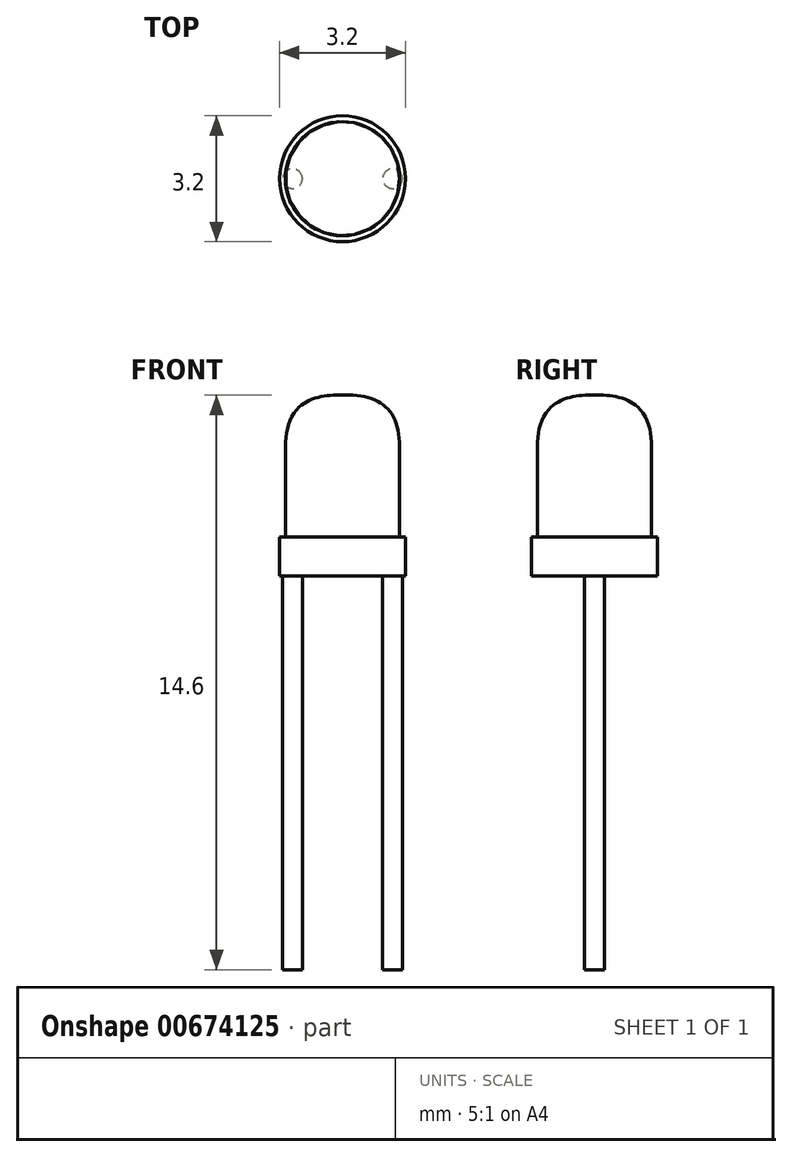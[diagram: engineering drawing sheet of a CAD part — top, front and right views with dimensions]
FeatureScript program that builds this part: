
annotation { "Feature Type Name" : "Feature", "Feature Type Description" : "" }
export const myFeature = defineFeature(function(context is Context, id is Id, definition is map)
    precondition{}
    {
        {
            var Q0;
            Q0=qCreatedBy(makeId("Top.planeOp"),FACE);
            var sketch = newSketch(context, id + "F0", { "sketchPlane" : qUnion([Q0])});
            skCircle(sketch, "E0", {"center": v(0, 0) * mm, "radius": 1.6 * mm});
            skCircle(sketch, "E1", {"center": v(0, 0) * mm, "radius": 1.45 * mm});
            skCircle(sketch, "E2", {"center": v(-1.27, 0) * mm, "radius": 0.25 * mm});
            skCircle(sketch, "E3", {"center": v(1.27, 0) * mm, "radius": 0.25 * mm});
            skSolve(sketch);
        }
        {
            var Q0;
            Q0=makeQuery(id+"F0.imprint","IMPRINT",FACE,{"disambiguationData":[TD([[makeQuery(id+"F0.imprint","IMPRINT",EDGE,{"derivedFrom":sQuery(id+"F0.wireOp",EDGE,"E0")}),1.0]])]});
            var Q1;
            {var subQ0=sQuery(id+"F0.wireOp",EDGE,"E2");var subQ1=sQuery(id+"F0.wireOp",EDGE,"E1");var subQ2=makeQuery(id+"F0.imprint","INTERSECT",VERTEX,{"disambiguationData":[OD(0.0)],"derivedFrom":[subQ1,subQ0]});Q1=makeQuery(id+"F0.imprint","IMPRINT",FACE,{"disambiguationData":[TD([[makeQuery(id+"F0.imprint","IMPRINT",EDGE,{"disambiguationData":[TD([[subQ2,1.0]])],"derivedFrom":subQ1}),1.0]])]});}
            var Q2;
            {var subQ0=sQuery(id+"F0.wireOp",EDGE,"E2");var subQ1=sQuery(id+"F0.wireOp",EDGE,"E1");var subQ2=makeQuery(id+"F0.imprint","INTERSECT",VERTEX,{"disambiguationData":[OD(0.0)],"derivedFrom":[subQ1,subQ0]});Q2=makeQuery(id+"F0.imprint","IMPRINT",FACE,{"disambiguationData":[TD([[makeQuery(id+"F0.imprint","IMPRINT",EDGE,{"disambiguationData":[TD([[subQ2,-1.0]])],"derivedFrom":subQ1}),1.0]])]});}
            var Q3;
            {var subQ0=sQuery(id+"F0.wireOp",EDGE,"E3");var subQ1=sQuery(id+"F0.wireOp",EDGE,"E1");var subQ2=makeQuery(id+"F0.imprint","INTERSECT",VERTEX,{"disambiguationData":[OD(0.0)],"derivedFrom":[subQ1,subQ0]});Q3=makeQuery(id+"F0.imprint","IMPRINT",FACE,{"disambiguationData":[TD([[makeQuery(id+"F0.imprint","IMPRINT",EDGE,{"disambiguationData":[TD([[subQ2,1.0]])],"derivedFrom":subQ1}),1.0]])]});}
            var Q4;
            {var subQ0=sQuery(id+"F0.wireOp",EDGE,"E3");var subQ1=sQuery(id+"F0.wireOp",EDGE,"E1");var subQ2=makeQuery(id+"F0.imprint","INTERSECT",VERTEX,{"disambiguationData":[OD(0.0)],"derivedFrom":[subQ1,subQ0]});Q4=makeQuery(id+"F0.imprint","IMPRINT",FACE,{"disambiguationData":[TD([[makeQuery(id+"F0.imprint","IMPRINT",EDGE,{"disambiguationData":[TD([[subQ2,1.0]])],"derivedFrom":subQ1}),-1.0]])]});}
            var Q5;
            {var subQ0=sQuery(id+"F0.wireOp",EDGE,"E2");var subQ1=sQuery(id+"F0.wireOp",EDGE,"E1");var subQ2=makeQuery(id+"F0.imprint","INTERSECT",VERTEX,{"disambiguationData":[OD(0.0)],"derivedFrom":[subQ1,subQ0]});Q5=makeQuery(id+"F0.imprint","IMPRINT",FACE,{"disambiguationData":[TD([[makeQuery(id+"F0.imprint","IMPRINT",EDGE,{"disambiguationData":[TD([[subQ2,-1.0]])],"derivedFrom":subQ1}),-1.0]])]});}
            extrude(context, id + "F1", {"entities" : qUnion([Q0, Q1, Q2, Q3, Q4, Q5]), "depth" : 1 * mm, "offsetDistance" : 25 * mm});
        }
        {
            var Q0;
            {var subQ0=sQuery(id+"F0.wireOp",EDGE,"E2");var subQ1=sQuery(id+"F0.wireOp",EDGE,"E1");var subQ2=makeQuery(id+"F0.imprint","INTERSECT",VERTEX,{"disambiguationData":[OD(0.0)],"derivedFrom":[subQ1,subQ0]});Q0=makeQuery(id+"F0.imprint","IMPRINT",FACE,{"disambiguationData":[TD([[makeQuery(id+"F0.imprint","IMPRINT",EDGE,{"disambiguationData":[TD([[subQ2,-1.0]])],"derivedFrom":subQ1}),-1.0]])]});}
            var Q1;
            {var subQ0=sQuery(id+"F0.wireOp",EDGE,"E2");var subQ1=sQuery(id+"F0.wireOp",EDGE,"E1");var subQ2=makeQuery(id+"F0.imprint","INTERSECT",VERTEX,{"disambiguationData":[OD(0.0)],"derivedFrom":[subQ1,subQ0]});Q1=makeQuery(id+"F0.imprint","IMPRINT",FACE,{"disambiguationData":[TD([[makeQuery(id+"F0.imprint","IMPRINT",EDGE,{"disambiguationData":[TD([[subQ2,-1.0]])],"derivedFrom":subQ1}),1.0]])]});}
            var Q2;
            {var subQ0=sQuery(id+"F0.wireOp",EDGE,"E3");var subQ1=sQuery(id+"F0.wireOp",EDGE,"E1");var subQ2=makeQuery(id+"F0.imprint","INTERSECT",VERTEX,{"disambiguationData":[OD(0.0)],"derivedFrom":[subQ1,subQ0]});Q2=makeQuery(id+"F0.imprint","IMPRINT",FACE,{"disambiguationData":[TD([[makeQuery(id+"F0.imprint","IMPRINT",EDGE,{"disambiguationData":[TD([[subQ2,1.0]])],"derivedFrom":subQ1}),1.0]])]});}
            var Q3;
            {var subQ0=sQuery(id+"F0.wireOp",EDGE,"E3");var subQ1=sQuery(id+"F0.wireOp",EDGE,"E1");var subQ2=makeQuery(id+"F0.imprint","INTERSECT",VERTEX,{"disambiguationData":[OD(0.0)],"derivedFrom":[subQ1,subQ0]});Q3=makeQuery(id+"F0.imprint","IMPRINT",FACE,{"disambiguationData":[TD([[makeQuery(id+"F0.imprint","IMPRINT",EDGE,{"disambiguationData":[TD([[subQ2,1.0]])],"derivedFrom":subQ1}),-1.0]])]});}
            extrude(context, id + "F2", {"entities" : qUnion([Q0, Q1, Q2, Q3]), "operationType" : NewBodyOperationType.ADD, "depth" : -10 * mm, "offsetDistance" : 25 * mm});
        }
        {
            var Q0;
            {var subQ0=sQuery(id+"F0.wireOp",EDGE,"E2");var subQ1=sQuery(id+"F0.wireOp",EDGE,"E1");var subQ2=makeQuery(id+"F0.imprint","INTERSECT",VERTEX,{"disambiguationData":[OD(0.0)],"derivedFrom":[subQ1,subQ0]});Q0=makeQuery(id+"F0.imprint","IMPRINT",FACE,{"disambiguationData":[TD([[makeQuery(id+"F0.imprint","IMPRINT",EDGE,{"disambiguationData":[TD([[subQ2,-1.0]])],"derivedFrom":subQ1}),1.0]])]});}
            var Q1;
            {var subQ0=sQuery(id+"F0.wireOp",EDGE,"E3");var subQ1=sQuery(id+"F0.wireOp",EDGE,"E1");var subQ2=makeQuery(id+"F0.imprint","INTERSECT",VERTEX,{"disambiguationData":[OD(0.0)],"derivedFrom":[subQ1,subQ0]});Q1=makeQuery(id+"F0.imprint","IMPRINT",FACE,{"disambiguationData":[TD([[makeQuery(id+"F0.imprint","IMPRINT",EDGE,{"disambiguationData":[TD([[subQ2,1.0]])],"derivedFrom":subQ1}),1.0]])]});}
            var Q2;
            {var subQ0=sQuery(id+"F0.wireOp",EDGE,"E2");var subQ1=sQuery(id+"F0.wireOp",EDGE,"E1");var subQ2=makeQuery(id+"F0.imprint","INTERSECT",VERTEX,{"disambiguationData":[OD(0.0)],"derivedFrom":[subQ1,subQ0]});Q2=makeQuery(id+"F0.imprint","IMPRINT",FACE,{"disambiguationData":[TD([[makeQuery(id+"F0.imprint","IMPRINT",EDGE,{"disambiguationData":[TD([[subQ2,1.0]])],"derivedFrom":subQ1}),1.0]])]});}
            extrude(context, id + "F3", {"entities" : qUnion([Q0, Q1, Q2]), "operationType" : NewBodyOperationType.ADD, "depth" : 4.6 * mm, "offsetDistance" : 25 * mm});
        }
        {
            var Q0;
            Q0=makeQuery(id+"F3.opExtrude","CAP_FACE",FACE,{"disambiguationData":[OSD([sQuery(id+"F0.wireOp",EDGE,"E1")])],"isStart":false});
            fillet(context, id + "F4", {"entities" : qUnion([Q0]), "radius" : 1.3 * mm, "tangentPropagation" : true, "rho" : 0.5, "crossSection" : FilletCrossSection.CONIC, "allowEdgeOverflow" : false});
        }
    });
